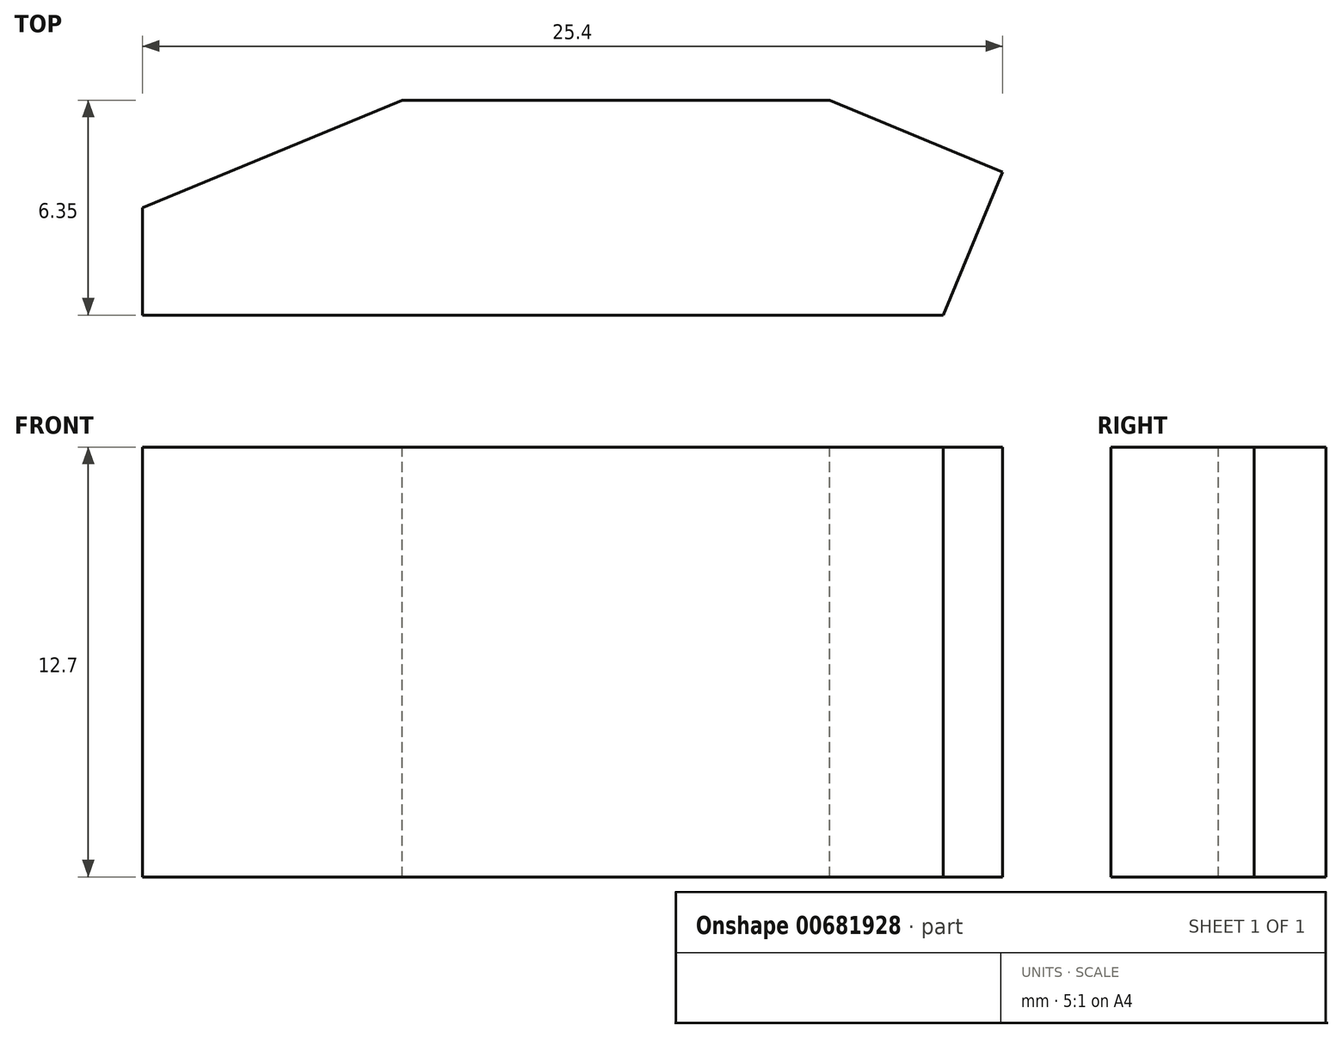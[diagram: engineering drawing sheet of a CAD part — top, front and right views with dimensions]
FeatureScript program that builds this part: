
annotation { "Feature Type Name" : "Feature", "Feature Type Description" : "" }
export const myFeature = defineFeature(function(context is Context, id is Id, definition is map)
    precondition{}
    {
        {
            var Q0;
            Q0=qCreatedBy(makeId("Right.planeOp"),FACE);
            var sketch = newSketch(context, id + "F0", { "sketchPlane" : qUnion([Q0])});
            skLineSegment(sketch, "E0.bottom", {"start": v(3.17, 6.35) * mm, "end": v(-3.18, 6.35) * mm});
            skLineSegment(sketch, "E0.top", {"start": v(3.17, -6.35) * mm, "end": v(-3.18, -6.35) * mm});
            skLineSegment(sketch, "E0.left", {"start": v(3.18, 6.35) * mm, "end": v(3.17, -6.35) * mm});
            skLineSegment(sketch, "E0.right", {"start": v(-3.18, 6.35) * mm, "end": v(-3.18, -6.35) * mm});
            skPoint(sketch, "E0.middle", {"position": v(0, 0) * mm});
            skSolve(sketch);
        }
        {
            var Q0;
            Q0=qSketchRegion(id+"F0",true);
            extrude(context, id + "F1", {"entities" : qUnion([Q0]), "depth" : 25.4 * mm, "offsetDistance" : 25.4 * mm, "symmetric" : true});
        }
        {
            var Q0;
            Q0=qCreatedBy(makeId("Top.planeOp"),FACE);
            var sketch = newSketch(context, id + "F2", { "sketchPlane" : qUnion([Q0])});
            skLineSegment(sketch, "E1", {"start": v(-12.7, 0) * mm, "end": v(-5.03, 3.17) * mm});
            skLineSegment(sketch, "E2.0", {"start": v(-12.7, 3.17) * mm, "end": v(-12.7, 0) * mm});
            skLineSegment(sketch, "E3.0.1", {"start": v(-12.7, -3.18) * mm, "end": v(12.7, -3.18) * mm});
            skLineSegment(sketch, "E3.0.3", {"start": v(-5.03, 3.17) * mm, "end": v(-12.7, 3.17) * mm});
            skLineSegment(sketch, "E4.0.1", {"start": v(-12.7, -3.18) * mm, "end": v(12.7, -3.18) * mm, "construction": true});
            skLineSegment(sketch, "E5.0.2", {"start": v(12.7, -3.18) * mm, "end": v(12.7, 3.17) * mm, "construction": true});
            skSolve(sketch);
        }
        {
            var Q0;
            Q0=qSketchRegion(id+"F2",true);
            extrude(context, id + "F3", {"entities" : qUnion([Q0]), "operationType" : NewBodyOperationType.REMOVE, "endBound" : BoundingType.THROUGH_ALL, "oppositeDirection" : true, "depth" : 25.4 * mm, "offsetDistance" : 25.4 * mm, "hasSecondDirection" : true, "secondDirectionBound" : BoundingType.THROUGH_ALL, "secondDirectionOppositeDirection" : false, "secondDirectionDepth" : 25.4 * mm});
        }
        {
            var Q0;
            Q0=qCreatedBy(makeId("Top.planeOp"),FACE);
            var sketch = newSketch(context, id + "F4", { "sketchPlane" : qUnion([Q0])});
            skLineSegment(sketch, "E6", {"start": v(7.6, 3.17) * mm, "end": v(12.7, 1.06) * mm});
            skLineSegment(sketch, "E7", {"start": v(7.6, 3.17) * mm, "end": v(17.97, 3.17) * mm});
            skLineSegment(sketch, "E8", {"start": v(17.97, 3.17) * mm, "end": v(12.7, 1.06) * mm});
            skSolve(sketch);
        }
        {
            var Q0;
            Q0 = qSketchRegion(id + "F4", true);
            extrude(context, id + "F5", {"entities" : qUnion([Q0]), "operationType" : NewBodyOperationType.REMOVE, "endBound" : BoundingType.THROUGH_ALL, "oppositeDirection" : true, "depth" : 25.4 * mm, "offsetDistance" : 25.4 * mm, "hasSecondDirection" : true, "secondDirectionBound" : BoundingType.THROUGH_ALL, "secondDirectionOppositeDirection" : false, "secondDirectionDepth" : 25.4 * mm});
        }
        {
            var Q0;
            Q0=qCreatedBy(makeId("Top.planeOp"),FACE);
            var sketch = newSketch(context, id + "F6", { "sketchPlane" : qUnion([Q0])});
            skLineSegment(sketch, "E9", {"start": v(10.95, -3.18) * mm, "end": v(12.7, 1.06) * mm});
            skLineSegment(sketch, "E10.0", {"start": v(12.7, 1.06) * mm, "end": v(12.7, -3.18) * mm});
            skLineSegment(sketch, "E11.0", {"start": v(12.7, -3.18) * mm, "end": v(10.95, -3.18) * mm});
            skPoint(sketch, "E12.orphan", {"position": v(-5.03, -3.18) * mm});
            skSolve(sketch);
        }
        {
            var Q0;
            Q0 = qSketchRegion(id + "F6", true);
            extrude(context, id + "F7", {"entities" : qUnion([Q0]), "operationType" : NewBodyOperationType.REMOVE, "endBound" : BoundingType.THROUGH_ALL, "oppositeDirection" : true, "depth" : 25.4 * mm, "offsetDistance" : 25.4 * mm, "hasSecondDirection" : true, "secondDirectionBound" : BoundingType.THROUGH_ALL, "secondDirectionOppositeDirection" : false, "secondDirectionDepth" : 25.4 * mm});
        }
    });
